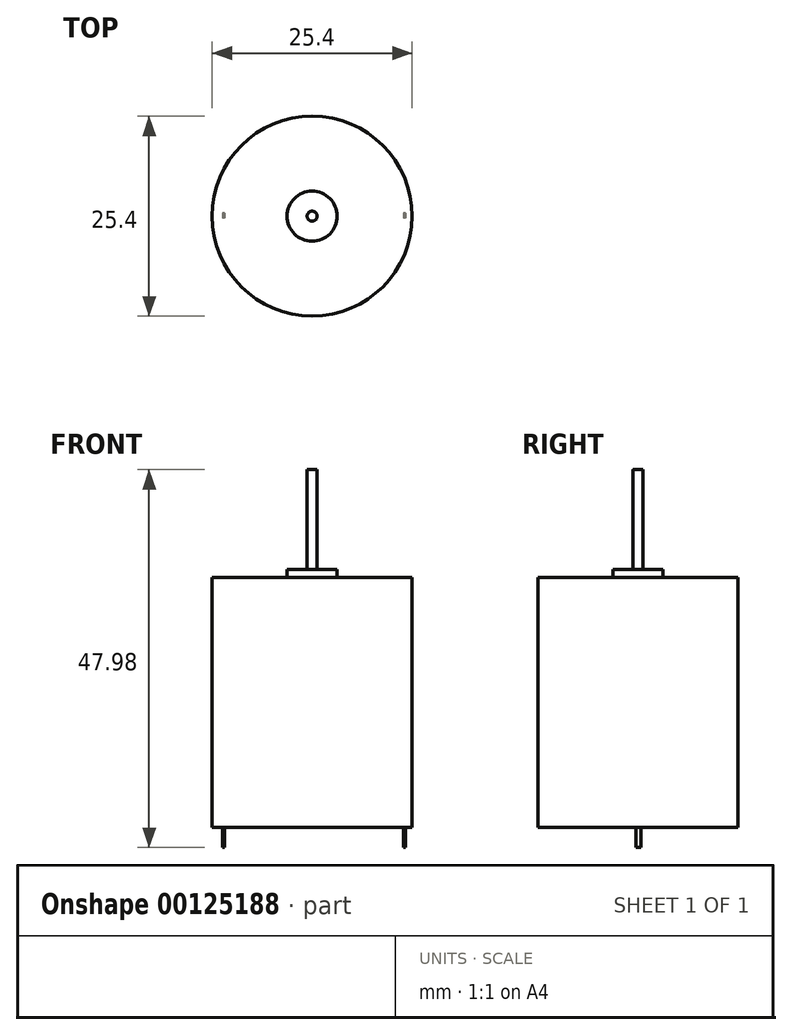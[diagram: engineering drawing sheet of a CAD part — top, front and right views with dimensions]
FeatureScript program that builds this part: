
annotation { "Feature Type Name" : "Feature", "Feature Type Description" : "" }
export const myFeature = defineFeature(function(context is Context, id is Id, definition is map)
    precondition{}
    {
        {
            var Q0;
            Q0=qCreatedBy(makeId("Top.planeOp"),FACE);
            var sketch = newSketch(context, id + "F0", { "sketchPlane" : qUnion([Q0])});
            skCircle(sketch, "E0", {"center": v(0, 0) * mm, "radius": 12.7 * mm});
            skSolve(sketch);
        }
        {
            var Q0;
            Q0 = qSketchRegion(id + "F0", true);
            extrude(context, id + "F1", {"entities" : qUnion([Q0]), "depth" : 31.75 * mm});
        }
        {
            var Q0;
            Q0=makeQuery(id+"F1.opExtrude","CAP_FACE",FACE,{"disambiguationData":[OSD([sQuery(id+"F0.wireOp",EDGE,"E0")])],"isStart":false});
            var sketch = newSketch(context, id + "F2", { "sketchPlane" : qUnion([Q0])});
            skCircle(sketch, "E1", {"center": v(0, 0) * mm, "radius": 3.18 * mm});
            skSolve(sketch);
        }
        {
            var Q0;
            Q0 = qSketchRegion(id + "F2", true);
            extrude(context, id + "F3", {"entities" : qUnion([Q0]), "operationType" : NewBodyOperationType.ADD, "depth" : 0.99 * mm});
        }
        {
            var Q0;
            Q0=makeQuery(id+"F3.opExtrude","CAP_FACE",FACE,{"disambiguationData":[OSD([sQuery(id+"F2.wireOp",EDGE,"E1")])],"isStart":false});
            var sketch = newSketch(context, id + "F4", { "sketchPlane" : qUnion([Q0])});
            skCircle(sketch, "E2", {"center": v(0, 0) * mm, "radius": 0.64 * mm});
            skSolve(sketch);
        }
        {
            var Q0;
            Q0=makeQuery(id+"F4.imprint","IMPRINT",FACE,{"disambiguationData":[TD([[makeQuery(id+"F4.imprint","IMPRINT",EDGE,{"derivedFrom":sQuery(id+"F4.wireOp",EDGE,"E2")}),1.0]])]});
            extrude(context, id + "F5", {"entities" : qUnion([Q0]), "depth" : 12.7 * mm});
        }
        {
            var Q0;
            Q0=makeQuery(id+"F1.opExtrude","CAP_FACE",FACE,{"disambiguationData":[OSD([sQuery(id+"F0.wireOp",EDGE,"E0")])],"isStart":true});
            var sketch = newSketch(context, id + "F6", { "sketchPlane" : qUnion([Q0])});
            skLineSegment(sketch, "E3.bottom", {"start": v(11.83, -0.37) * mm, "end": v(11.58, -0.37) * mm});
            skLineSegment(sketch, "E3.top", {"start": v(11.83, 0.26) * mm, "end": v(11.58, 0.26) * mm});
            skLineSegment(sketch, "E3.left", {"start": v(11.83, -0.37) * mm, "end": v(11.83, 0.26) * mm});
            skLineSegment(sketch, "E3.right", {"start": v(11.58, -0.37) * mm, "end": v(11.58, 0.26) * mm});
            skLineSegment(sketch, "E4.bottom", {"start": v(-11.1, -0.37) * mm, "end": v(-11.35, -0.37) * mm});
            skLineSegment(sketch, "E4.top", {"start": v(-11.1, 0.26) * mm, "end": v(-11.35, 0.26) * mm});
            skLineSegment(sketch, "E4.left", {"start": v(-11.1, -0.37) * mm, "end": v(-11.1, 0.26) * mm});
            skLineSegment(sketch, "E4.right", {"start": v(-11.35, -0.37) * mm, "end": v(-11.35, 0.26) * mm});
            skSolve(sketch);
        }
        {
            var Q0;
            Q0 = qSketchRegion(id + "F6", true);
            extrude(context, id + "F7", {"entities" : qUnion([Q0]), "operationType" : NewBodyOperationType.ADD, "depth" : 2.54 * mm});
        }
    });
